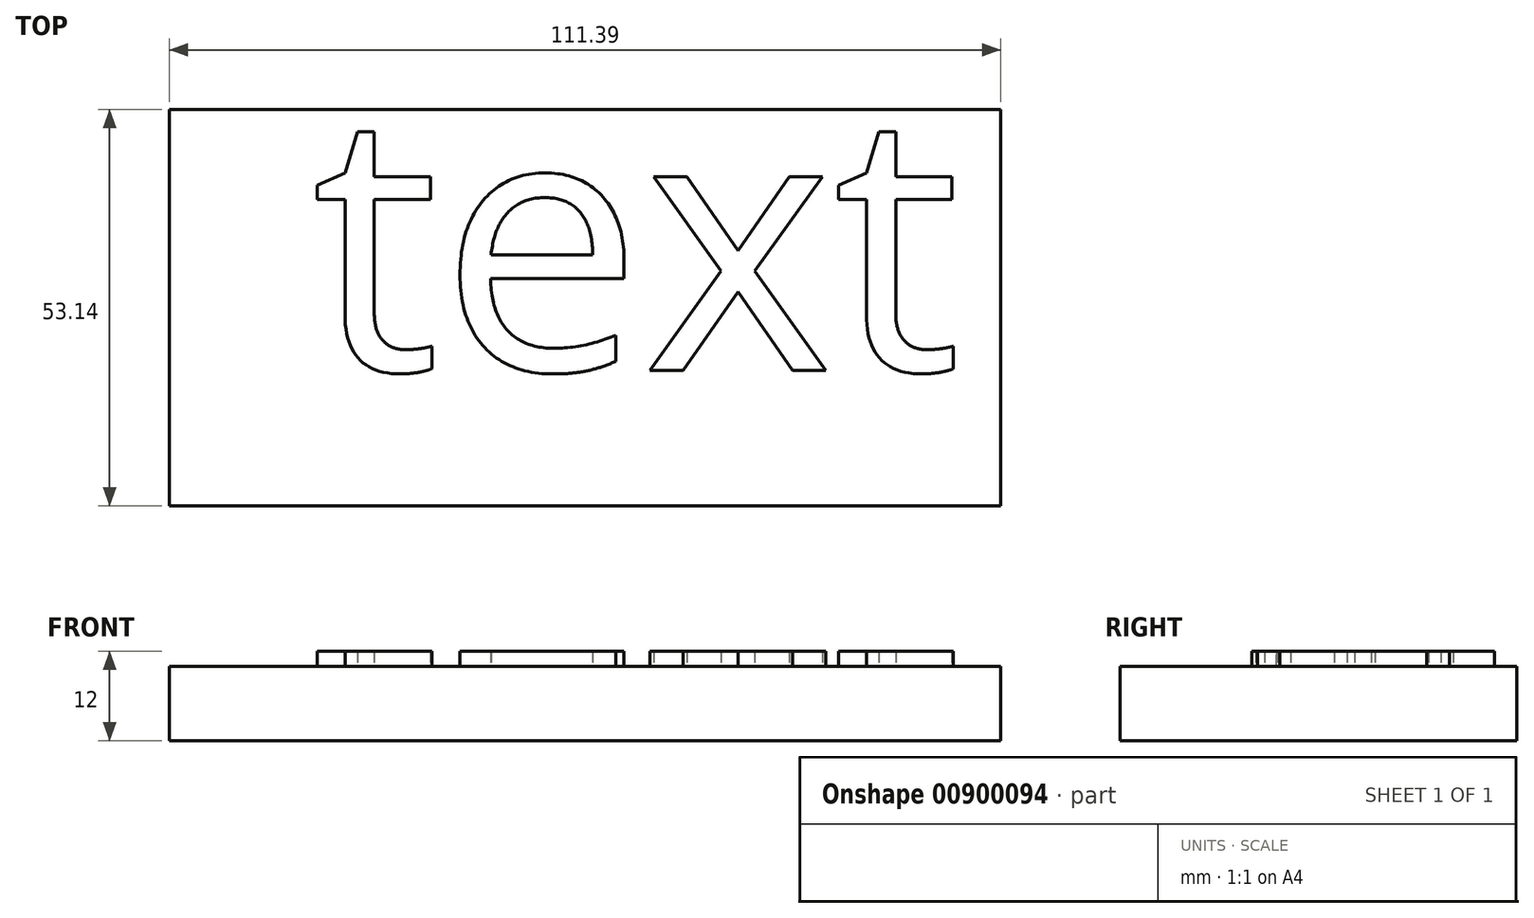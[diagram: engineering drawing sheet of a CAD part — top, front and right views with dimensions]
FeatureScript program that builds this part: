
annotation { "Feature Type Name" : "Feature", "Feature Type Description" : "" }
export const myFeature = defineFeature(function(context is Context, id is Id, definition is map)
    precondition{}
    {
        {
            var Q0;
            Q0=qCreatedBy(makeId("Top.planeOp"),FACE);
            var sketch = newSketch(context, id + "F0", { "sketchPlane" : qUnion([Q0])});
            skLineSegment(sketch, "E0.bottom", {"start": v(-56.04, 34.98) * mm, "end": v(55.35, 34.98) * mm});
            skLineSegment(sketch, "E0.top", {"start": v(-56.04, -18.16) * mm, "end": v(55.35, -18.16) * mm});
            skLineSegment(sketch, "E0.left", {"start": v(-56.04, 34.98) * mm, "end": v(-56.04, -18.16) * mm});
            skLineSegment(sketch, "E0.right", {"start": v(55.35, 34.98) * mm, "end": v(55.35, -18.16) * mm});
            skSolve(sketch);
        }
        {
            var Q0;
            Q0 = qSketchRegion(id + "F0", true);
            extrude(context, id + "F1", {"entities" : qUnion([Q0]), "depth" : 10 * mm, "offsetDistance" : 25 * mm});
        }
        {
            var Q0;
            Q0=makeQuery(id+"F1.opExtrude","CAP_FACE",FACE,{"disambiguationData":[OSD([sQuery(id+"F0.wireOp",EDGE,"E0.bottom"),sQuery(id+"F0.wireOp",EDGE,"E0.top"),sQuery(id+"F0.wireOp",EDGE,"E0.left"),sQuery(id+"F0.wireOp",EDGE,"E0.right")])],"isStart":false});
            var sketch = newSketch(context, id + "F2", { "sketchPlane" : qUnion([Q0])});
            skText(sketch, "E1", { "text": "text\n", "fontName": "OpenSans-Regular.ttf"});
            const initialGuessF2  = {"E1": [-0.03696, 0, 1, 0, 0.03498]};
            skSetInitialGuess(sketch, initialGuessF2);
            skSolve(sketch);
        }
        {
            var Q0;
            Q0 = qSketchRegion(id + "F2", true);
            extrude(context, id + "F3", {"entities" : qUnion([Q0]), "operationType" : NewBodyOperationType.ADD, "depth" : 2 * mm, "offsetDistance" : 25 * mm});
        }
    });
